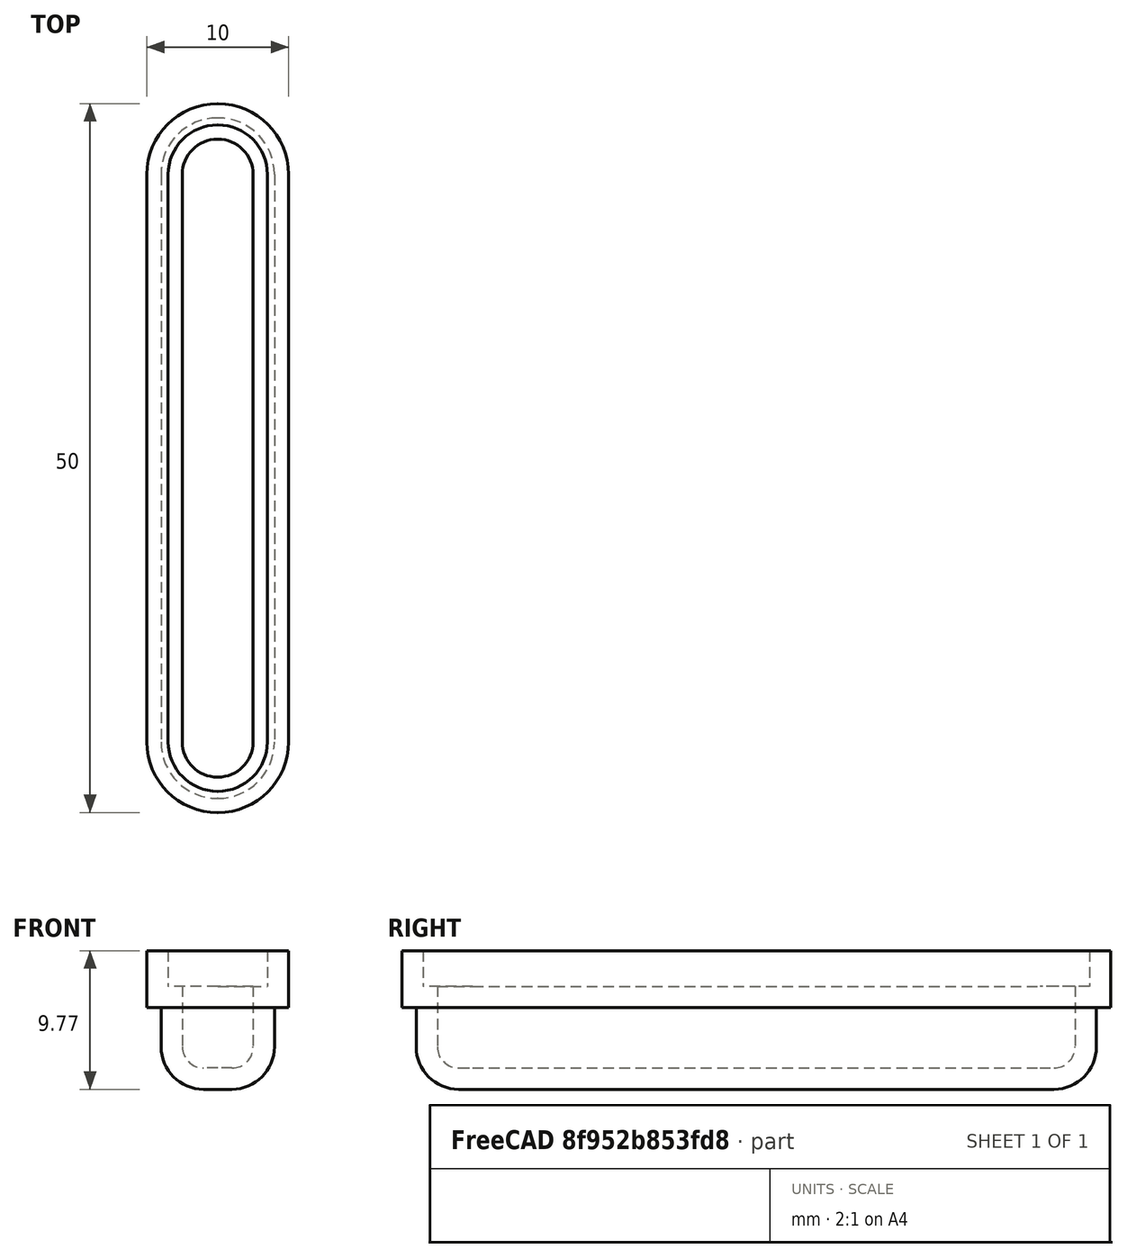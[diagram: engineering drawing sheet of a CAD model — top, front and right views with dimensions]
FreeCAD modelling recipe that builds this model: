
FCSTD DOCUMENT  (FreeCAD 0.20R29410 (Git))
Label: LED Cover
License: All rights reserved
LicenseURL: http://en.wikipedia.org/wiki/All_rights_reserved
objects: PartDesign::Fillet×3, PartDesign::AdditiveBox×2, PartDesign::Thickness×1, PartDesign::Body×1
note: 13 computed .brp shape members not serialized (recipe doc carries the construction recipe); baked Part::Feature solids carry a one-line shape summary decoded from their .brp

FEATURE [PartDesign::AdditiveBox] Box
  AttacherType = Attacher::AttachEngine3D
  Height = 4
  Length = 50
  MapMode = 5
  Support = -> [XY_Plane075]
  Width = 10
FEATURE [PartDesign::AdditiveBox] Box001
  AttacherType = Attacher::AttachEngine3D
  AttachmentOffset = pos=(1,1,0) rot=(0,0,1;0rad)
  BaseFeature = -> Box
  Height = 5.77
  Length = 48
  MapMode = 5
  Placement = pos=(1,1,4) rot=(0,0,1;0rad)
  Support = -> [Box]
  Width = 8
FEATURE [PartDesign::Fillet] Fillet003
  Base = -> Box001 [Edge20,Edge23,Edge19,Edge17]
  BaseFeature = -> Box001
  Placement = pos=(1,1,4) rot=(0,0,1;0rad)
  Radius = 3.99
  SupportTransform = false
  UseAllEdges = false
FEATURE [PartDesign::Fillet] Fillet004
  Base = -> Fillet003 [Face14]
  BaseFeature = -> Fillet003
  Placement = pos=(1,1,4) rot=(0,0,1;0rad)
  Radius = 3
  SupportTransform = false
  UseAllEdges = false
FEATURE [PartDesign::Fillet] Fillet005
  Base = -> Fillet004 [Edge47,Edge45,Edge42,Edge41]
  BaseFeature = -> Fillet004
  Placement = pos=(1,1,4) rot=(0,0,1;0rad)
  Radius = 4.99
  SupportTransform = false
  UseAllEdges = false
FEATURE [PartDesign::Thickness] Thickness
  Base = -> Fillet005 [Face18]
  BaseFeature = -> Fillet005
  Intersection = false
  Join = 1
  Mode = 0
  Reversed = true
  SupportTransform = false
  Value = 1.5
FEATURE [PartDesign::Body] Body001  label="LED cover"
  Group = -> [Box,Box001,Fillet003,Fillet004,Fillet005,Thickness]
  Origin = -> Origin075
  Placement = pos=(4.94,33.4,7.08) rot=(0.707107,-0.707107,0;3.14159rad)
  Tip = -> Thickness
